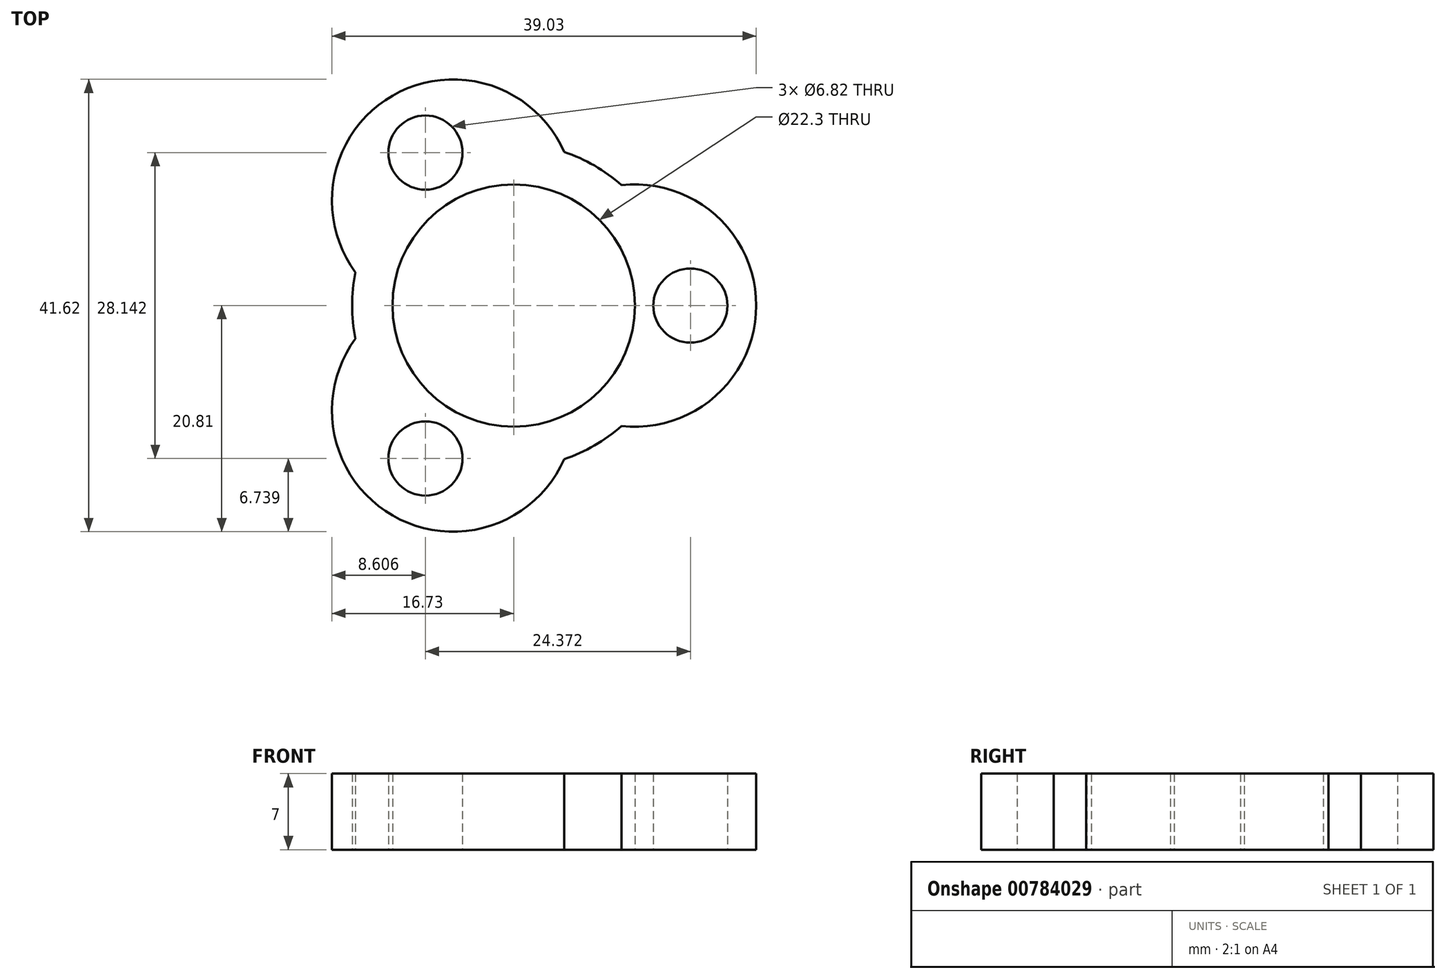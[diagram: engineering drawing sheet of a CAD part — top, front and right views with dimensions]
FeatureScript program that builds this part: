
annotation { "Feature Type Name" : "Feature", "Feature Type Description" : "" }
export const myFeature = defineFeature(function(context is Context, id is Id, definition is map)
    precondition{}
    {
        {
            var Q0;
            Q0=qCreatedBy(makeId("Top.planeOp"),FACE);
            var sketch = newSketch(context, id + "F0", { "sketchPlane" : qUnion([Q0])});
            skCircle(sketch, "E0", {"center": v(0, 0) * mm, "radius": 11.15 * mm});
            skArc(sketch, "E1", {"start": v(0, 0) * mm, "mid": v(-5.58, 20.8) * mm, "end": v(-11.15, 0) * mm});
            skArc(sketch, "E2.1.0", {"start": v(0, 0) * mm, "mid": v(-15.23, -15.23) * mm, "end": v(5.58, -9.66) * mm});
            skArc(sketch, "E2.2.0", {"start": v(0, 0) * mm, "mid": v(20.8, -5.57) * mm, "end": v(5.57, 9.66) * mm});
            skArc(sketch, "E3", {"start": v(4.64, -14.12) * mm, "mid": v(7.43, -12.87) * mm, "end": v(9.91, -11.08) * mm});
            skArc(sketch, "E4.1.0", {"start": v(9.91, 11.08) * mm, "mid": v(7.43, 12.87) * mm, "end": v(4.64, 14.12) * mm});
            skArc(sketch, "E4.2.0", {"start": v(-14.55, 3.04) * mm, "mid": v(-14.87, 0) * mm, "end": v(-14.55, -3.04) * mm});
            skCircle(sketch, "E5", {"center": v(16.25, 0) * mm, "radius": 3.41 * mm});
            skCircle(sketch, "E6.1.0", {"center": v(-8.12, 14.07) * mm, "radius": 3.41 * mm});
            skCircle(sketch, "E6.2.0", {"center": v(-8.12, -14.07) * mm, "radius": 3.41 * mm});
            skSolve(sketch);
        }
        {
            var Q0;
            Q0=makeQuery(id+"F0.imprint","IMPRINT",FACE,{"disambiguationData":[TD([[makeQuery(id+"F0.imprint","IMPRINT",EDGE,{"derivedFrom":sQuery(id+"F0.wireOp",EDGE,"E6.1.0")}),-1.0]])]});
            var Q1;
            {var subQ3=sQuery(id+"F0.wireOp",EDGE,"E4.2.0");Q1=makeQuery(id+"F0.imprint","IMPRINT",FACE,{"disambiguationData":[TD([[makeQuery(id+"F0.imprint","IMPRINT",EDGE,{"derivedFrom":subQ3}),1.0]])]});}
            var Q2;
            Q2=makeQuery(id+"F0.imprint","IMPRINT",FACE,{"disambiguationData":[TD([[makeQuery(id+"F0.imprint","IMPRINT",EDGE,{"derivedFrom":sQuery(id+"F0.wireOp",EDGE,"E6.2.0")}),-1.0]])]});
            var Q3;
            {var subQ3=sQuery(id+"F0.wireOp",EDGE,"E3");Q3=makeQuery(id+"F0.imprint","IMPRINT",FACE,{"disambiguationData":[TD([[makeQuery(id+"F0.imprint","IMPRINT",EDGE,{"derivedFrom":subQ3}),1.0]])]});}
            var Q4;
            Q4=makeQuery(id+"F0.imprint","IMPRINT",FACE,{"disambiguationData":[TD([[makeQuery(id+"F0.imprint","IMPRINT",EDGE,{"derivedFrom":sQuery(id+"F0.wireOp",EDGE,"E5")}),-1.0]])]});
            var Q5;
            {var subQ3=sQuery(id+"F0.wireOp",EDGE,"E4.1.0");Q5=makeQuery(id+"F0.imprint","IMPRINT",FACE,{"disambiguationData":[TD([[makeQuery(id+"F0.imprint","IMPRINT",EDGE,{"derivedFrom":subQ3}),1.0]])]});}
            extrude(context, id + "F1", {"entities" : qUnion([Q0, Q1, Q2, Q3, Q4, Q5]), "depth" : 7 * mm, "offsetDistance" : 25 * mm});
        }
    });
